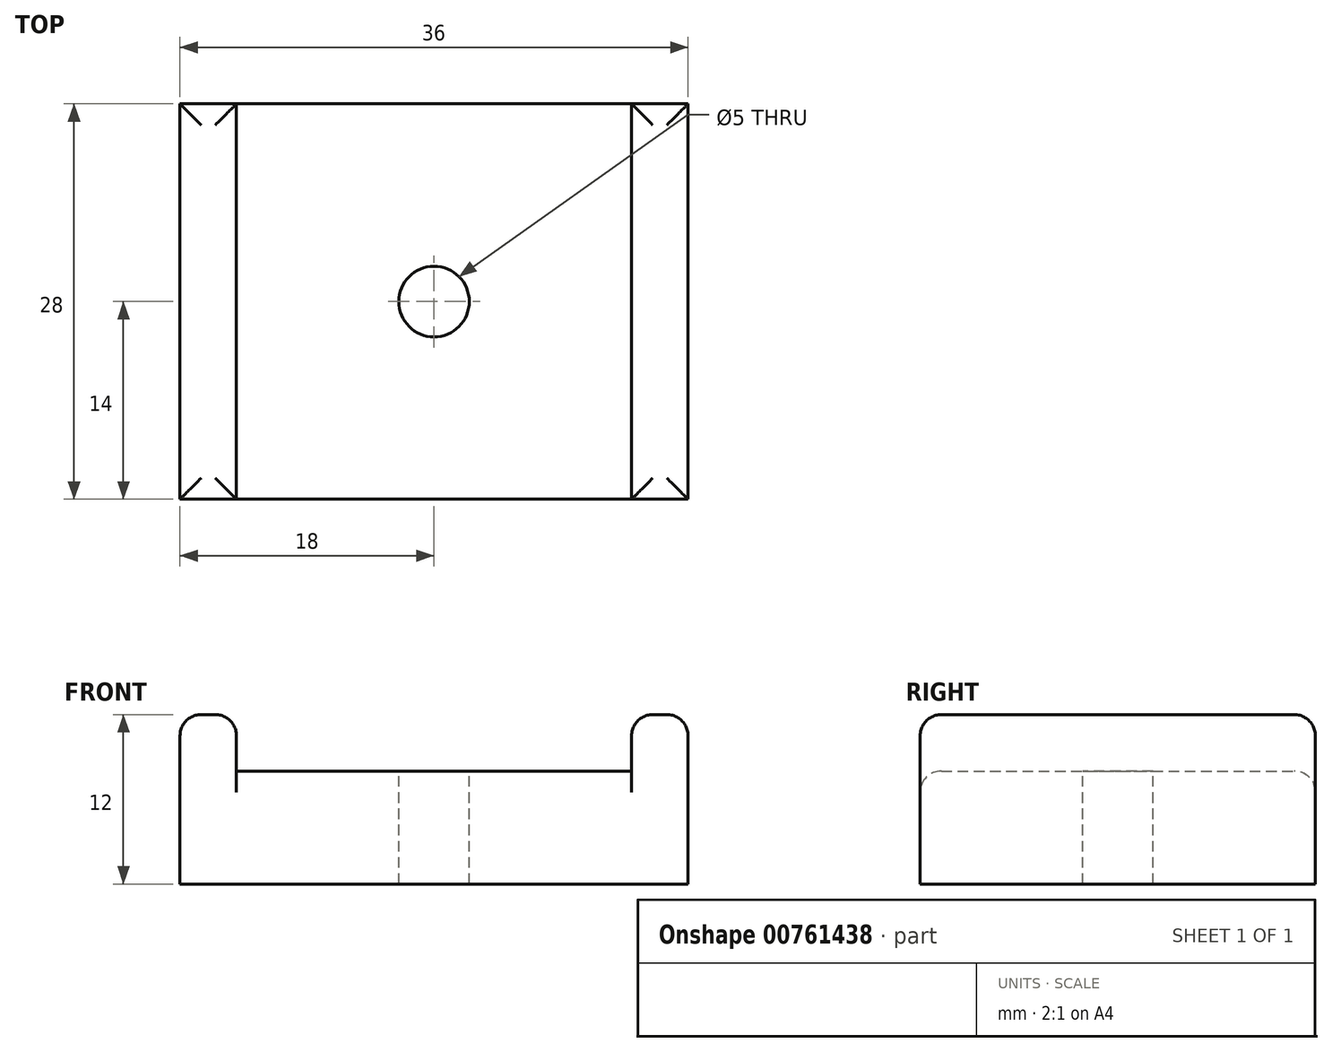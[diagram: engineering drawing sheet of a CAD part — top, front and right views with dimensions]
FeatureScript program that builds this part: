
annotation { "Feature Type Name" : "Feature", "Feature Type Description" : "" }
export const myFeature = defineFeature(function(context is Context, id is Id, definition is map)
    precondition{}
    {
        {
            var Q0;
            Q0=qCreatedBy(makeId("Top.planeOp"),FACE);
            var sketch = newSketch(context, id + "F0", { "sketchPlane" : qUnion([Q0])});
            skLineSegment(sketch, "E0.bottom", {"start": v(0, 0) * mm, "end": v(-14, 0) * mm});
            skLineSegment(sketch, "E0.top", {"start": v(0, 28) * mm, "end": v(-14, 28) * mm});
            skLineSegment(sketch, "E0.left", {"start": v(0, 0) * mm, "end": v(0, 28) * mm});
            skLineSegment(sketch, "E0.right", {"start": v(-14, 0) * mm, "end": v(-14, 28) * mm});
            skLineSegment(sketch, "E1.bottom", {"start": v(-14, 28) * mm, "end": v(-18, 28) * mm});
            skLineSegment(sketch, "E1.top", {"start": v(-14, 0) * mm, "end": v(-18, 0) * mm});
            skLineSegment(sketch, "E1.left", {"start": v(-14, 28) * mm, "end": v(-14, 0) * mm});
            skLineSegment(sketch, "E1.right", {"start": v(-18, 28) * mm, "end": v(-18, 0) * mm});
            skLineSegment(sketch, "E2.MirrorCS", {"start": v(14, 0) * mm, "end": v(14, 28) * mm});
            skLineSegment(sketch, "E3.MirrorCS", {"start": v(0, 28) * mm, "end": v(14, 28) * mm});
            skLineSegment(sketch, "E4.MirrorCS", {"start": v(18, 28) * mm, "end": v(18, 0) * mm});
            skLineSegment(sketch, "E5.MirrorCS", {"start": v(0, 0) * mm, "end": v(0, 28) * mm, "construction": true});
            skLineSegment(sketch, "E6.MirrorCS", {"start": v(0, 0) * mm, "end": v(14, 0) * mm});
            skLineSegment(sketch, "E7.MirrorCS", {"start": v(14, 28) * mm, "end": v(14, 0) * mm});
            skLineSegment(sketch, "E8.MirrorCS", {"start": v(14, 0) * mm, "end": v(18, 0) * mm});
            skLineSegment(sketch, "E9.MirrorCS", {"start": v(14, 28) * mm, "end": v(18, 28) * mm});
            skPoint(sketch, "E10", {"position": v(0, 14) * mm});
            skSolve(sketch);
        }
        {
            var Q0;
            Q0=makeQuery(id+"F0.imprint","IMPRINT",FACE,{"disambiguationData":[TD([[makeQuery(id+"F0.imprint","IMPRINT",EDGE,{"derivedFrom":sQuery(id+"F0.wireOp",EDGE,"E0.bottom")}),-1.0]])]});
            var Q1;
            Q1=makeQuery(id+"F0.imprint","IMPRINT",FACE,{"disambiguationData":[TD([[makeQuery(id+"F0.imprint","IMPRINT",EDGE,{"derivedFrom":sQuery(id+"F0.wireOp",EDGE,"E0.left")}),-1.0]])]});
            extrude(context, id + "F1", {"entities" : qUnion([Q0, Q1]), "depth" : 8 * mm, "offsetDistance" : 25 * mm});
        }
        {
            var Q0;
            Q0=makeQuery(id+"F0.imprint","IMPRINT",FACE,{"disambiguationData":[TD([[makeQuery(id+"F0.imprint","IMPRINT",EDGE,{"derivedFrom":sQuery(id+"F0.wireOp",EDGE,"E1.bottom")}),1.0]])]});
            var Q1;
            Q1=makeQuery(id+"F0.imprint","IMPRINT",FACE,{"disambiguationData":[TD([[makeQuery(id+"F0.imprint","IMPRINT",EDGE,{"derivedFrom":sQuery(id+"F0.wireOp",EDGE,"E4.MirrorCS")}),-1.0]])]});
            extrude(context, id + "F2", {"entities" : qUnion([Q0, Q1]), "operationType" : NewBodyOperationType.ADD, "depth" : 12 * mm, "offsetDistance" : 25 * mm});
        }
        {
            var Q0;
            Q0=sQuery(id+"F0.wireOp",VERTEX,"E10");
            var Q1;
            Q1=makeQuery(id+"F1.opExtrude","SWEPT_BODY",BODY,{"disambiguationData":[OSD([sQuery(id+"F0.wireOp",EDGE,"E0.bottom"),sQuery(id+"F0.wireOp",EDGE,"E0.top"),sQuery(id+"F0.wireOp",EDGE,"E1.left"),sQuery(id+"F0.wireOp",EDGE,"E3.MirrorCS"),sQuery(id+"F0.wireOp",EDGE,"E6.MirrorCS"),sQuery(id+"F0.wireOp",EDGE,"E7.MirrorCS")])]});
            hole(context, id + "F3", {"style" : HoleStyle.SIMPLE, "endStyle" : HoleEndStyle.THROUGH, "oppositeDirection" : true, "holeDiameter" : 5 * mm, "majorDiameter" : 5 * mm, "isTappedThrough" : true, "tappedDepth" : 12 * mm, "tapClearance" : 3, "locations" : qUnion([Q0]), "scope" : qUnion([Q1]), "startStyle" : HoleStartStyle.PART});
        }
        {
            var Q0;
            Q0=makeQuery(id+"F2.opExtrude","CAP_FACE",FACE,{"disambiguationData":[OSD([sQuery(id+"F0.wireOp",EDGE,"E1.bottom"),sQuery(id+"F0.wireOp",EDGE,"E1.top"),sQuery(id+"F0.wireOp",EDGE,"E1.left"),sQuery(id+"F0.wireOp",EDGE,"E1.right")])],"isStart":false});
            var Q1;
            Q1=makeQuery(id+"F2.opExtrude","CAP_FACE",FACE,{"disambiguationData":[OSD([sQuery(id+"F0.wireOp",EDGE,"E4.MirrorCS"),sQuery(id+"F0.wireOp",EDGE,"E7.MirrorCS"),sQuery(id+"F0.wireOp",EDGE,"E8.MirrorCS"),sQuery(id+"F0.wireOp",EDGE,"E9.MirrorCS")])],"isStart":false});
            var Q2;
            Q2=makeQuery(id+"F1.opExtrude","CAP_EDGE",EDGE,{"disambiguationData":[OSD([sQuery(id+"F0.wireOp",EDGE,"E0.top"),sQuery(id+"F0.wireOp",EDGE,"E3.MirrorCS")])],"isStart":false});
            var Q3;
            Q3=makeQuery(id+"F1.opExtrude","CAP_EDGE",EDGE,{"disambiguationData":[OSD([sQuery(id+"F0.wireOp",EDGE,"E0.bottom"),sQuery(id+"F0.wireOp",EDGE,"E6.MirrorCS")])],"isStart":false});
            fillet(context, id + "F4", {"entities" : qUnion([Q0, Q1, Q2, Q3]), "radius" : 1.5 * mm, "tangentPropagation" : true, "allowEdgeOverflow" : false});
        }
    });
